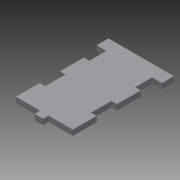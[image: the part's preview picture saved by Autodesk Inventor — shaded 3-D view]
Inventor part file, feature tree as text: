
AUTODESK INVENTOR PART (.ipt)
format: ipt  version: 2013 (Build 170138000, 138)  size: 118,784 bytes
history: native  units: mm
features: other x2, extrude x1, sketch x1
ambient origin geometry x8: Origin, YZ Plane, XZ Plane, XY Plane, X Axis, Y Axis, Z Axis, Center Point
feature tree (4):
  other  "Blocks"
  extrude  "Extrusion2"  Depth=3.0mm
  sketch  "Sketch1"  dims[d0=3.0mm d2=3.0mm d3=0.1mm d4=38.5mm d6=7.0mm d7=22.5mm d8=12.4mm d9=4.5mm d10=4.5mm d11=2.0mm d12=2.0mm d17=27.0mm d20=50.0mm d23=3.25mm d24=14.0mm d25=10.0mm d26=3.25mm d27=14.0mm d28=5.0mm d29=3.25mm d30=3.25mm d31=0.0mm]
  other  "Block1"
